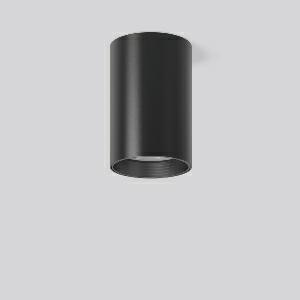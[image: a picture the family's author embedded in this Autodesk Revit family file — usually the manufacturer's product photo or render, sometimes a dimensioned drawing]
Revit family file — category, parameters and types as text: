
# Revit family: heledon_maxi_a_931248_003_2_76_4155
name_source: partatom
category: Lighting Fixtures
units: mm (PartAtom-declared; Revit-internal decimal feet)

## family parameters
Cut with Voids When Loaded = No
Host = Face
Light Source = No
Part Type = Normal
Room Calculation Point = No
Round Connector Dimension = Use Diameter
Shared = No

## types (1)
- HELEDON maxi A (1 x LED Modul 927 bakery, 2950 lm, 2700)
    Apparent Load = 33 VA
    Approval mark = CE
    CIE Flux Codes = 97 100 100 100 100
    Color Rendering = 90
    Color Temperature = 2700
    Default Elevation = 1800 mm
    Description = Series: HELEDON maxi
Cylindrical surface-mounted downlight. Housing: die-cast aluminium, powder-coated. Internal ceiling frame polycarbonate with bayonet mounting. Black plastic ring and recessed LED to prevent glare from the side. Optical assembly with lens made of plastic (polycarbonate) for the best homogeneous light distribution - can be changed without tools. Special LED for illumination of pastries included. Suitable for Ceiling mounting. Easy installation with a separate ceiling frame with bayonet mounting and plug connection. Driver integrated. Connected via plug-in connector. High quality converter without flickering and stroboscopic effect. The following accessories can be mounted without use of tools: interchangeable lenses, decorative glasses, honeycomb louvre, clear and frosted diffusers, white interchangeable plastic ring. 
Colour: deep black, matt (RAL 9005)
Diameter: 123 mm
Height: 183 mm
Lamp: LED
Socket: without socket
Colour temperature: bakery
Colour rendering index (CRI): 97
System power: 33 W
Rated luminous flux: 2950 lm
Luminous efficiency: 89 lm/W
Control gear: Converter, dimmable, DALI
Protection class: I
Type of protection: IP 20
    Height = 183 mm
    Lamp = 1 x LED Modul 927 bakery
    Lamp Light Flux = 2950 lm
    Lamp count = 1
    Length = 123 mm
    Lifetime = 50000 h
    Luminous efficacy = 89 lm/W
    Manufacturer = RZB
    ModVariant = No
    Model = 931248.003.2.76
    Mounting Place = Ceiling
    Mounting Type = Surface mounted
    Number of Poles = 1
    OnlyDefault = Yes
    Power Factor = 1
    Product Name = HELEDON maxi A
    Product group = Surface mounted downlights
    ProductGroupID = 302
    Protection Class = Protection class I
    Protection Degree = IP 20
    RLX_Detail_Level = 1
    RLX_Emergency_Light_Flux = 0 lm
    RLX_Emergency_Type = 0
    RLX_Emergency_Type_DB = No
    RlxData = <blob elided: 97097 chars, md5=2d767ffd>
    Socket = socket
    Standby Power = 0 W
    System Light Flux = 2950 lm
    System Power = 33 W
    Type Comments = Product without accessories
    Type Image = 931193.003.jpg
    URL = http://relux.com
    VarID = ---
    Voltage = 230 V
    Voltage Range = 220-240 V
    Weight = 0.00 kg
    Width = 0 mm  [stored 0 ft]

note: [stored X ft] marks values corroborated as IEEE doubles in the binary element streams (Revit-internal decimal feet)

## geometry (parser evidence)
native form markers: Blend x4, Sweep x12
no freeform markers — native parametric forms only
